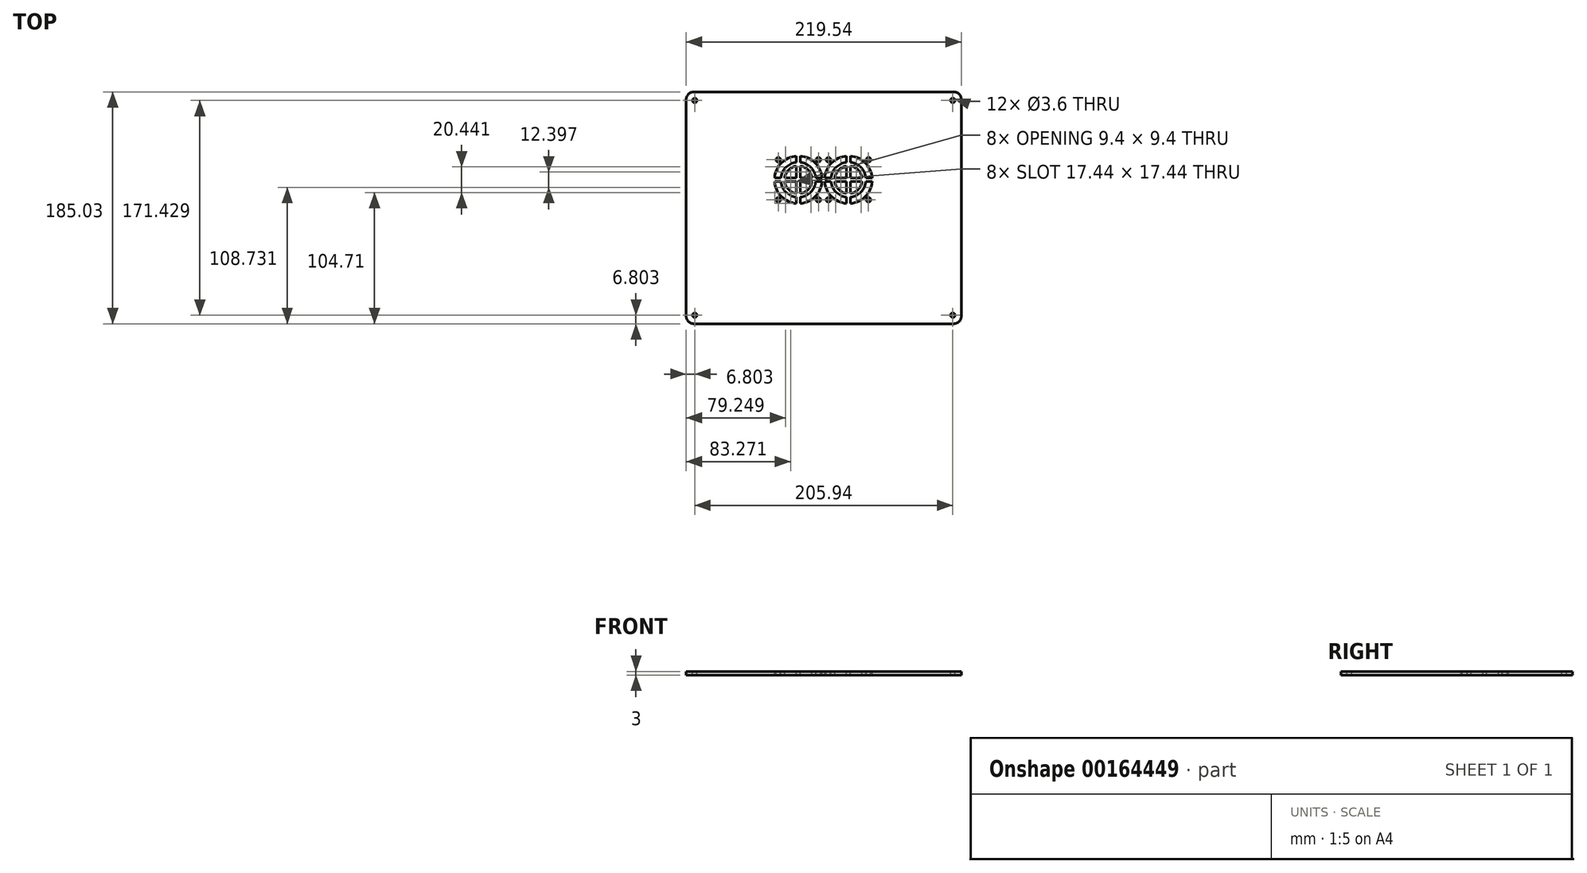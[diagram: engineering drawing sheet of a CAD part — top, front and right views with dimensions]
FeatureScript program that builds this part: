
annotation { "Feature Type Name" : "Feature", "Feature Type Description" : "" }
export const myFeature = defineFeature(function(context is Context, id is Id, definition is map)
    precondition{}
    {
        {
            var Q0;
            Q0=qCreatedBy(makeId("Top.planeOp"),FACE);
            var sketch = newSketch(context, id + "F0", { "sketchPlane" : qUnion([Q0])});
            skLineSegment(sketch, "E0.bottom", {"start": v(-112.37, 119.3) * mm, "end": v(107.17, 119.3) * mm});
            skLineSegment(sketch, "E0.top", {"start": v(-112.37, -65.74) * mm, "end": v(107.17, -65.74) * mm});
            skLineSegment(sketch, "E0.left", {"start": v(-112.37, 119.3) * mm, "end": v(-112.37, -65.74) * mm});
            skLineSegment(sketch, "E0.right", {"start": v(107.17, 119.3) * mm, "end": v(107.17, -65.74) * mm});
            skSolve(sketch);
        }
        {
            var Q0;
            Q0=makeQuery(id+"F0.imprint","IMPRINT",FACE,{"disambiguationData":[TD([[makeQuery(id+"F0.imprint","IMPRINT",EDGE,{"derivedFrom":sQuery(id+"F0.wireOp",EDGE,"E0.bottom")}),-1.0]])]});
            extrude(context, id + "F1", {"entities" : qUnion([Q0]), "depth" : 3 * mm});
        }
        {
            var Q0;
            Q0=makeQuery(id+"F1.opExtrude","CAP_FACE",FACE,{"disambiguationData":[OSD([sQuery(id+"F0.wireOp",EDGE,"E0.bottom"),sQuery(id+"F0.wireOp",EDGE,"E0.top"),sQuery(id+"F0.wireOp",EDGE,"E0.left"),sQuery(id+"F0.wireOp",EDGE,"E0.right")])],"isStart":false});
            var sketch = newSketch(context, id + "F2", { "sketchPlane" : qUnion([Q0])});
            skLineSegment(sketch, "E1.bottom", {"start": v(-42.9, 69.19) * mm, "end": v(-2.9, 69.19) * mm});
            skLineSegment(sketch, "E1.top", {"start": v(-42.9, 29.19) * mm, "end": v(-2.9, 29.19) * mm});
            skLineSegment(sketch, "E1.left", {"start": v(-42.9, 69.19) * mm, "end": v(-42.9, 29.19) * mm});
            skLineSegment(sketch, "E1.right", {"start": v(-2.9, 69.19) * mm, "end": v(-2.9, 29.19) * mm});
            skLineSegment(sketch, "E2.bottom", {"start": v(-2.9, 29.19) * mm, "end": v(37.1, 29.19) * mm});
            skLineSegment(sketch, "E2.top", {"start": v(-2.9, 69.19) * mm, "end": v(37.1, 69.19) * mm});
            skLineSegment(sketch, "E2.left", {"start": v(-2.9, 29.19) * mm, "end": v(-2.9, 69.19) * mm});
            skLineSegment(sketch, "E2.right", {"start": v(37.1, 29.19) * mm, "end": v(37.1, 69.19) * mm});
            skCircle(sketch, "E3", {"center": v(-38.9, 65.19) * mm, "radius": 1.8 * mm});
            skCircle(sketch, "E4", {"center": v(-6.9, 65.19) * mm, "radius": 1.8 * mm});
            skCircle(sketch, "E5", {"center": v(-38.9, 33.19) * mm, "radius": 1.8 * mm});
            skCircle(sketch, "E6", {"center": v(-6.9, 33.19) * mm, "radius": 1.8 * mm});
            skCircle(sketch, "E7", {"center": v(1.1, 65.19) * mm, "radius": 1.8 * mm});
            skCircle(sketch, "E8", {"center": v(33.1, 65.19) * mm, "radius": 1.8 * mm});
            skCircle(sketch, "E9", {"center": v(33.1, 33.19) * mm, "radius": 1.8 * mm});
            skCircle(sketch, "E10", {"center": v(1.1, 33.19) * mm, "radius": 1.8 * mm});
            skPoint(sketch, "E11", {"position": v(-22.9, 69.19) * mm});
            skPoint(sketch, "E12", {"position": v(17.1, 69.19) * mm});
            skPoint(sketch, "E13", {"position": v(-2.9, 49.19) * mm});
            skPoint(sketch, "E14", {"position": v(-22.9, 49.19) * mm});
            skPoint(sketch, "E15", {"position": v(17.1, 49.19) * mm});
            skCircle(sketch, "E16", {"center": v(-22.9, 49.19) * mm, "radius": 19 * mm});
            skCircle(sketch, "E17", {"center": v(17.1, 49.19) * mm, "radius": 19 * mm});
            skArc(sketch, "E18", {"start": v(-36.82, 47.69) * mm, "mid": v(-32.8, 39.3) * mm, "end": v(-24.4, 35.27) * mm});
            skArc(sketch, "E19", {"start": v(-33.8, 47.69) * mm, "mid": v(-30.68, 41.41) * mm, "end": v(-24.4, 38.3) * mm});
            skLineSegment(sketch, "E20.left", {"start": v(-21.4, 30.25) * mm, "end": v(-21.4, 35.27) * mm});
            skLineSegment(sketch, "E20.right", {"start": v(-24.4, 30.25) * mm, "end": v(-24.4, 35.27) * mm});
            skLineSegment(sketch, "E21.bottom", {"start": v(-41.84, 50.69) * mm, "end": v(-36.82, 50.69) * mm});
            skLineSegment(sketch, "E21.top", {"start": v(-41.84, 47.69) * mm, "end": v(-36.82, 47.69) * mm});
            skLineSegment(sketch, "E22.trimOffspring", {"start": v(-24.4, 50.69) * mm, "end": v(-24.4, 60.09) * mm});
            skLineSegment(sketch, "E23.trimOffspring", {"start": v(-21.4, 50.69) * mm, "end": v(-12, 50.69) * mm});
            skLineSegment(sketch, "E24.trimOffspring", {"start": v(-21.4, 50.69) * mm, "end": v(-21.4, 60.09) * mm});
            skLineSegment(sketch, "E25.trimOffspring", {"start": v(-21.4, 47.69) * mm, "end": v(-12, 47.69) * mm});
            skLineSegment(sketch, "E26.trimOffspring", {"start": v(-33.8, 50.69) * mm, "end": v(-24.4, 50.69) * mm});
            skLineSegment(sketch, "E27.trimOffspring", {"start": v(-33.8, 47.69) * mm, "end": v(-24.4, 47.69) * mm});
            skLineSegment(sketch, "E28.trimOffspring", {"start": v(-24.4, 38.3) * mm, "end": v(-24.4, 47.69) * mm});
            skLineSegment(sketch, "E29.trimOffspring", {"start": v(-21.4, 38.3) * mm, "end": v(-21.4, 47.69) * mm});
            skArc(sketch, "E30.trimOffspring", {"start": v(-21.4, 38.3) * mm, "mid": v(-15.12, 41.41) * mm, "end": v(-12, 47.69) * mm});
            skArc(sketch, "E31.trimOffspring", {"start": v(-21.4, 35.27) * mm, "mid": v(-13, 39.3) * mm, "end": v(-8.98, 47.69) * mm});
            skArc(sketch, "E32.trimOffspring", {"start": v(-24.4, 60.09) * mm, "mid": v(-30.68, 56.97) * mm, "end": v(-33.8, 50.69) * mm});
            skLineSegment(sketch, "E33.trimOffspring", {"start": v(-21.4, 63.1) * mm, "end": v(-21.4, 68.13) * mm});
            skArc(sketch, "E34.trimOffspring", {"start": v(-24.4, 63.1) * mm, "mid": v(-32.8, 59.09) * mm, "end": v(-36.82, 50.69) * mm});
            skLineSegment(sketch, "E35.trimOffspring", {"start": v(-24.4, 63.1) * mm, "end": v(-24.4, 68.13) * mm});
            skArc(sketch, "E36.trimOffspring", {"start": v(-12, 50.69) * mm, "mid": v(-15.12, 56.97) * mm, "end": v(-21.4, 60.09) * mm});
            skLineSegment(sketch, "E37.trimOffspring", {"start": v(-8.98, 50.69) * mm, "end": v(-3.96, 50.69) * mm});
            skArc(sketch, "E38.trimOffspring", {"start": v(-8.98, 50.69) * mm, "mid": v(-13, 59.09) * mm, "end": v(-21.4, 63.1) * mm});
            skLineSegment(sketch, "E39.trimOffspring", {"start": v(-8.98, 47.69) * mm, "end": v(-3.96, 47.69) * mm});
            skArc(sketch, "E40", {"start": v(3.18, 47.69) * mm, "mid": v(7.2, 39.3) * mm, "end": v(15.6, 35.27) * mm});
            skArc(sketch, "E41", {"start": v(6.2, 47.69) * mm, "mid": v(9.32, 41.41) * mm, "end": v(15.6, 38.3) * mm});
            skLineSegment(sketch, "E42.left", {"start": v(15.6, 68.13) * mm, "end": v(15.6, 63.1) * mm});
            skLineSegment(sketch, "E42.right", {"start": v(18.6, 68.13) * mm, "end": v(18.6, 63.1) * mm});
            skLineSegment(sketch, "E43.bottom", {"start": v(36.04, 47.69) * mm, "end": v(31.02, 47.69) * mm});
            skLineSegment(sketch, "E43.top", {"start": v(36.04, 50.69) * mm, "end": v(31.02, 50.69) * mm});
            skLineSegment(sketch, "E44.trimOffspring", {"start": v(3.18, 50.69) * mm, "end": v(-1.84, 50.69) * mm});
            skLineSegment(sketch, "E45.trimOffspring", {"start": v(3.18, 47.69) * mm, "end": v(-1.84, 47.69) * mm});
            skLineSegment(sketch, "E46.trimOffspring", {"start": v(15.6, 47.69) * mm, "end": v(15.6, 38.3) * mm});
            skLineSegment(sketch, "E47.trimOffspring", {"start": v(15.6, 47.69) * mm, "end": v(6.2, 47.69) * mm});
            skLineSegment(sketch, "E48.trimOffspring", {"start": v(18.6, 47.69) * mm, "end": v(18.6, 38.3) * mm});
            skLineSegment(sketch, "E49.trimOffspring", {"start": v(15.6, 50.69) * mm, "end": v(6.2, 50.69) * mm});
            skArc(sketch, "E50.trimOffspring", {"start": v(28, 50.69) * mm, "mid": v(24.88, 56.97) * mm, "end": v(18.6, 60.09) * mm});
            skArc(sketch, "E51.trimOffspring", {"start": v(31.02, 50.69) * mm, "mid": v(27, 59.09) * mm, "end": v(18.6, 63.1) * mm});
            skLineSegment(sketch, "E52.trimOffspring", {"start": v(28, 50.69) * mm, "end": v(18.6, 50.69) * mm});
            skLineSegment(sketch, "E53.trimOffspring", {"start": v(28, 47.69) * mm, "end": v(18.6, 47.69) * mm});
            skArc(sketch, "E54.trimOffspring", {"start": v(18.6, 38.3) * mm, "mid": v(24.88, 41.41) * mm, "end": v(28, 47.69) * mm});
            skLineSegment(sketch, "E55.trimOffspring", {"start": v(15.6, 35.27) * mm, "end": v(15.6, 30.25) * mm});
            skArc(sketch, "E56.trimOffspring", {"start": v(18.6, 35.27) * mm, "mid": v(27, 39.3) * mm, "end": v(31.02, 47.69) * mm});
            skLineSegment(sketch, "E57.trimOffspring", {"start": v(18.6, 35.27) * mm, "end": v(18.6, 30.25) * mm});
            skLineSegment(sketch, "E58.trimOffspring", {"start": v(15.6, 60.09) * mm, "end": v(15.6, 50.69) * mm});
            skArc(sketch, "E59.trimOffspring", {"start": v(15.6, 63.1) * mm, "mid": v(7.2, 59.09) * mm, "end": v(3.18, 50.69) * mm});
            skLineSegment(sketch, "E60.trimOffspring", {"start": v(18.6, 60.09) * mm, "end": v(18.6, 50.69) * mm});
            skArc(sketch, "E61.trimOffspring", {"start": v(15.6, 60.09) * mm, "mid": v(9.32, 56.97) * mm, "end": v(6.2, 50.69) * mm});
            skCircle(sketch, "E62", {"center": v(-105.57, 112.5) * mm, "radius": 1.8 * mm});
            skPoint(sketch, "E63", {"position": v(-112.37, 119.3) * mm});
            skPoint(sketch, "E64", {"position": v(107.17, 119.3) * mm});
            skPoint(sketch, "E65", {"position": v(107.17, -65.74) * mm});
            skPoint(sketch, "E66", {"position": v(-112.37, -65.74) * mm});
            skCircle(sketch, "E67", {"center": v(100.37, 112.5) * mm, "radius": 1.8 * mm});
            skCircle(sketch, "E68", {"center": v(100.37, -58.94) * mm, "radius": 1.8 * mm});
            skCircle(sketch, "E69", {"center": v(-105.57, -58.94) * mm, "radius": 1.8 * mm});
            skSolve(sketch);
        }
        {
            var Q0;
            {var subQ0=sQuery(id+"F2.wireOp",EDGE,"E21.bottom");Q0=makeQuery(id+"F2.imprint","IMPRINT",FACE,{"disambiguationData":[TD([[makeQuery(id+"F2.imprint","IMPRINT",EDGE,{"derivedFrom":subQ0}),1.0]])]});}
            var Q1;
            Q1=makeQuery(id+"F2.imprint","IMPRINT",FACE,{"disambiguationData":[TD([[makeQuery(id+"F2.imprint","IMPRINT",EDGE,{"derivedFrom":sQuery(id+"F2.wireOp",EDGE,"E18")}),-1.0]])]});
            var Q2;
            {var subQ0=sQuery(id+"F2.wireOp",EDGE,"E20.left");Q2=makeQuery(id+"F2.imprint","IMPRINT",FACE,{"disambiguationData":[TD([[makeQuery(id+"F2.imprint","IMPRINT",EDGE,{"derivedFrom":subQ0}),-1.0]])]});}
            var Q3;
            Q3=makeQuery(id+"F2.imprint","IMPRINT",FACE,{"disambiguationData":[TD([[makeQuery(id+"F2.imprint","IMPRINT",EDGE,{"derivedFrom":sQuery(id+"F2.wireOp",EDGE,"E25.trimOffspring")}),-1.0]])]});
            var Q4;
            Q4=makeQuery(id+"F2.imprint","IMPRINT",FACE,{"disambiguationData":[TD([[makeQuery(id+"F2.imprint","IMPRINT",EDGE,{"derivedFrom":sQuery(id+"F2.wireOp",EDGE,"E19")}),1.0]])]});
            var Q5;
            Q5=makeQuery(id+"F2.imprint","IMPRINT",FACE,{"disambiguationData":[TD([[makeQuery(id+"F2.imprint","IMPRINT",EDGE,{"derivedFrom":sQuery(id+"F2.wireOp",EDGE,"E22.trimOffspring")}),1.0]])]});
            var Q6;
            {var subQ0=sQuery(id+"F2.wireOp",EDGE,"E33.trimOffspring");Q6=makeQuery(id+"F2.imprint","IMPRINT",FACE,{"disambiguationData":[TD([[makeQuery(id+"F2.imprint","IMPRINT",EDGE,{"derivedFrom":subQ0}),-1.0]])]});}
            var Q7;
            {var subQ0=sQuery(id+"F2.wireOp",EDGE,"E42.left");Q7=makeQuery(id+"F2.imprint","IMPRINT",FACE,{"disambiguationData":[TD([[makeQuery(id+"F2.imprint","IMPRINT",EDGE,{"derivedFrom":subQ0}),-1.0]])]});}
            var Q8;
            {var subQ0=sQuery(id+"F2.wireOp",EDGE,"E42.right");Q8=makeQuery(id+"F2.imprint","IMPRINT",FACE,{"disambiguationData":[TD([[makeQuery(id+"F2.imprint","IMPRINT",EDGE,{"derivedFrom":subQ0}),1.0]])]});}
            var Q9;
            Q9=makeQuery(id+"F2.imprint","IMPRINT",FACE,{"disambiguationData":[TD([[makeQuery(id+"F2.imprint","IMPRINT",EDGE,{"derivedFrom":sQuery(id+"F2.wireOp",EDGE,"E50.trimOffspring")}),1.0]])]});
            var Q10;
            Q10=makeQuery(id+"F2.imprint","IMPRINT",FACE,{"disambiguationData":[TD([[makeQuery(id+"F2.imprint","IMPRINT",EDGE,{"derivedFrom":sQuery(id+"F2.wireOp",EDGE,"E49.trimOffspring")}),-1.0]])]});
            var Q11;
            Q11=makeQuery(id+"F2.imprint","IMPRINT",FACE,{"disambiguationData":[TD([[makeQuery(id+"F2.imprint","IMPRINT",EDGE,{"derivedFrom":sQuery(id+"F2.wireOp",EDGE,"E41")}),1.0]])]});
            var Q12;
            Q12=makeQuery(id+"F2.imprint","IMPRINT",FACE,{"disambiguationData":[TD([[makeQuery(id+"F2.imprint","IMPRINT",EDGE,{"derivedFrom":sQuery(id+"F2.wireOp",EDGE,"E48.trimOffspring")}),1.0]])]});
            var Q13;
            Q13=makeQuery(id+"F2.imprint","IMPRINT",FACE,{"disambiguationData":[TD([[makeQuery(id+"F2.imprint","IMPRINT",EDGE,{"derivedFrom":sQuery(id+"F2.wireOp",EDGE,"E40")}),-1.0]])]});
            var Q14;
            {var subQ0=sQuery(id+"F2.wireOp",EDGE,"E43.bottom");Q14=makeQuery(id+"F2.imprint","IMPRINT",FACE,{"disambiguationData":[TD([[makeQuery(id+"F2.imprint","IMPRINT",EDGE,{"derivedFrom":subQ0}),1.0]])]});}
            var Q15;
            Q15=makeQuery(id+"F2.imprint","IMPRINT",FACE,{"disambiguationData":[TD([[makeQuery(id+"F2.imprint","IMPRINT",EDGE,{"derivedFrom":sQuery(id+"F2.wireOp",EDGE,"E23.trimOffspring")}),1.0]])]});
            var Q16;
            Q16=makeQuery(id+"F2.imprint","IMPRINT",FACE,{"disambiguationData":[TD([[makeQuery(id+"F2.imprint","IMPRINT",EDGE,{"derivedFrom":sQuery(id+"F2.wireOp",EDGE,"E3")}),1.0]])]});
            var Q17;
            Q17=makeQuery(id+"F2.imprint","IMPRINT",FACE,{"disambiguationData":[TD([[makeQuery(id+"F2.imprint","IMPRINT",EDGE,{"derivedFrom":sQuery(id+"F2.wireOp",EDGE,"E4")}),1.0]])]});
            var Q18;
            Q18=makeQuery(id+"F2.imprint","IMPRINT",FACE,{"disambiguationData":[TD([[makeQuery(id+"F2.imprint","IMPRINT",EDGE,{"derivedFrom":sQuery(id+"F2.wireOp",EDGE,"E7")}),1.0]])]});
            var Q19;
            Q19=makeQuery(id+"F2.imprint","IMPRINT",FACE,{"disambiguationData":[TD([[makeQuery(id+"F2.imprint","IMPRINT",EDGE,{"derivedFrom":sQuery(id+"F2.wireOp",EDGE,"E8")}),1.0]])]});
            var Q20;
            Q20=makeQuery(id+"F2.imprint","IMPRINT",FACE,{"disambiguationData":[TD([[makeQuery(id+"F2.imprint","IMPRINT",EDGE,{"derivedFrom":sQuery(id+"F2.wireOp",EDGE,"E9")}),1.0]])]});
            var Q21;
            Q21=makeQuery(id+"F2.imprint","IMPRINT",FACE,{"disambiguationData":[TD([[makeQuery(id+"F2.imprint","IMPRINT",EDGE,{"derivedFrom":sQuery(id+"F2.wireOp",EDGE,"E10")}),1.0]])]});
            var Q22;
            Q22=makeQuery(id+"F2.imprint","IMPRINT",FACE,{"disambiguationData":[TD([[makeQuery(id+"F2.imprint","IMPRINT",EDGE,{"derivedFrom":sQuery(id+"F2.wireOp",EDGE,"E6")}),1.0]])]});
            var Q23;
            Q23=makeQuery(id+"F2.imprint","IMPRINT",FACE,{"disambiguationData":[TD([[makeQuery(id+"F2.imprint","IMPRINT",EDGE,{"derivedFrom":sQuery(id+"F2.wireOp",EDGE,"E5")}),1.0]])]});
            var Q24;
            Q24=makeQuery(id+"F2.imprint","IMPRINT",FACE,{"disambiguationData":[TD([[makeQuery(id+"F2.imprint","IMPRINT",EDGE,{"derivedFrom":sQuery(id+"F2.wireOp",EDGE,"E69")}),1.0]])]});
            var Q25;
            Q25=makeQuery(id+"F2.imprint","IMPRINT",FACE,{"disambiguationData":[TD([[makeQuery(id+"F2.imprint","IMPRINT",EDGE,{"derivedFrom":sQuery(id+"F2.wireOp",EDGE,"E68")}),1.0]])]});
            var Q26;
            Q26=makeQuery(id+"F2.imprint","IMPRINT",FACE,{"disambiguationData":[TD([[makeQuery(id+"F2.imprint","IMPRINT",EDGE,{"derivedFrom":sQuery(id+"F2.wireOp",EDGE,"E67")}),1.0]])]});
            var Q27;
            Q27=makeQuery(id+"F2.imprint","IMPRINT",FACE,{"disambiguationData":[TD([[makeQuery(id+"F2.imprint","IMPRINT",EDGE,{"derivedFrom":sQuery(id+"F2.wireOp",EDGE,"E62")}),1.0]])]});
            extrude(context, id + "F3", {"entities" : qUnion([Q0, Q1, Q2, Q3, Q4, Q5, Q6, Q7, Q8, Q9, Q10, Q11, Q12, Q13, Q14, Q15, Q16, Q17, Q18, Q19, Q20, Q21, Q22, Q23, Q24, Q25, Q26, Q27]), "operationType" : NewBodyOperationType.REMOVE, "oppositeDirection" : true, "depth" : 25 * mm});
        }
        {
            var Q0;
            Q0=makeQuery(id+"F1.opExtrude","SWEPT_EDGE",EDGE,{"disambiguationData":[OSD([sQuery(id+"F0.wireOp",EDGE,"E0.bottom"),sQuery(id+"F0.wireOp",EDGE,"E0.left")])]});
            var Q1;
            Q1=makeQuery(id+"F1.opExtrude","SWEPT_EDGE",EDGE,{"disambiguationData":[OSD([sQuery(id+"F0.wireOp",EDGE,"E0.top"),sQuery(id+"F0.wireOp",EDGE,"E0.left")])]});
            var Q2;
            Q2=makeQuery(id+"F1.opExtrude","SWEPT_EDGE",EDGE,{"disambiguationData":[OSD([sQuery(id+"F0.wireOp",EDGE,"E0.top"),sQuery(id+"F0.wireOp",EDGE,"E0.right")])]});
            var Q3;
            Q3=makeQuery(id+"F1.opExtrude","SWEPT_EDGE",EDGE,{"disambiguationData":[OSD([sQuery(id+"F0.wireOp",EDGE,"E0.bottom"),sQuery(id+"F0.wireOp",EDGE,"E0.right")])]});
            fillet(context, id + "F4", {"entities" : qUnion([Q0, Q1, Q2, Q3]), "radius" : 6 * mm, "tangentPropagation" : true, "allowEdgeOverflow" : false});
        }
    });
